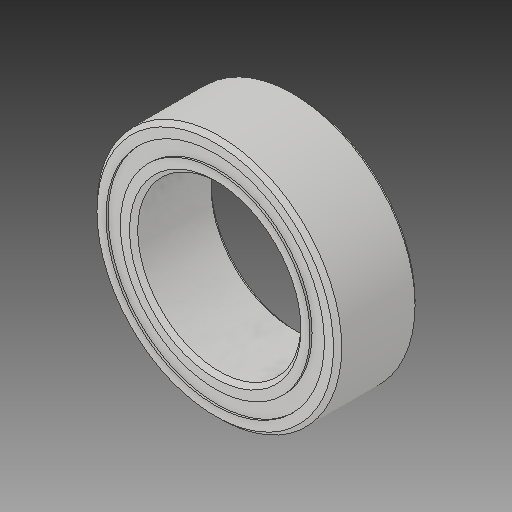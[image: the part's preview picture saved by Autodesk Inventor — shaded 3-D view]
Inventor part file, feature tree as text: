
AUTODESK INVENTOR PART (.ipt)
format: ipt  version: 2017 (Build 210142000, 142)  size: 611,840 bytes
history: native  units: in
note: dims shown in document units (in); Inventor stores cm internally (conversion verified against a paired STEP export)
features: other x11, revolve x5
ambient origin geometry x8: Origin, YZ Plane, XZ Plane, XY Plane, X Axis, Y Axis, Z Axis, Center Point
bodies: Solid1 (feature_tree), Solid2 (feature_tree), Solid3 (feature_tree), Solid4 (feature_tree), Solid5 (feature_tree), Solid6 (feature_tree), Solid7 (feature_tree), Solid8 (feature_tree), Solid9 (feature_tree), Solid10 (feature_tree), Solid11 (feature_tree), Solid12 (feature_tree), Solid13 (feature_tree), Solid14 (feature_tree), Solid15 (feature_tree), Solid16 (feature_tree)
feature tree (16):
  revolve  "Revolve1"  [1 undecoded]
  revolve  "Revolve3"  [1 undecoded]
  revolve  "Revolve4"  [1 undecoded]
  other  "CirPattern1[1]"
  other  "CirPattern1[2]"
  other  "CirPattern1[3]"
  other  "CirPattern1[4]"
  other  "CirPattern1[5]"
  other  "CirPattern1[6]"
  other  "CirPattern1[7]"
  other  "CirPattern1[8]"
  other  "CirPattern1[9]"
  other  "CirPattern1[10]"
  other  "CirPattern1[11]"
  revolve  "Revolve5[1]"  [1 undecoded]
  revolve  "Revolve5[2]"  [1 undecoded]
note: 5 required parameter values undecoded (feature->parameter linkage not recoverable at this tier; creation-order binding heuristic only, values carry confidence <= 0.55)
